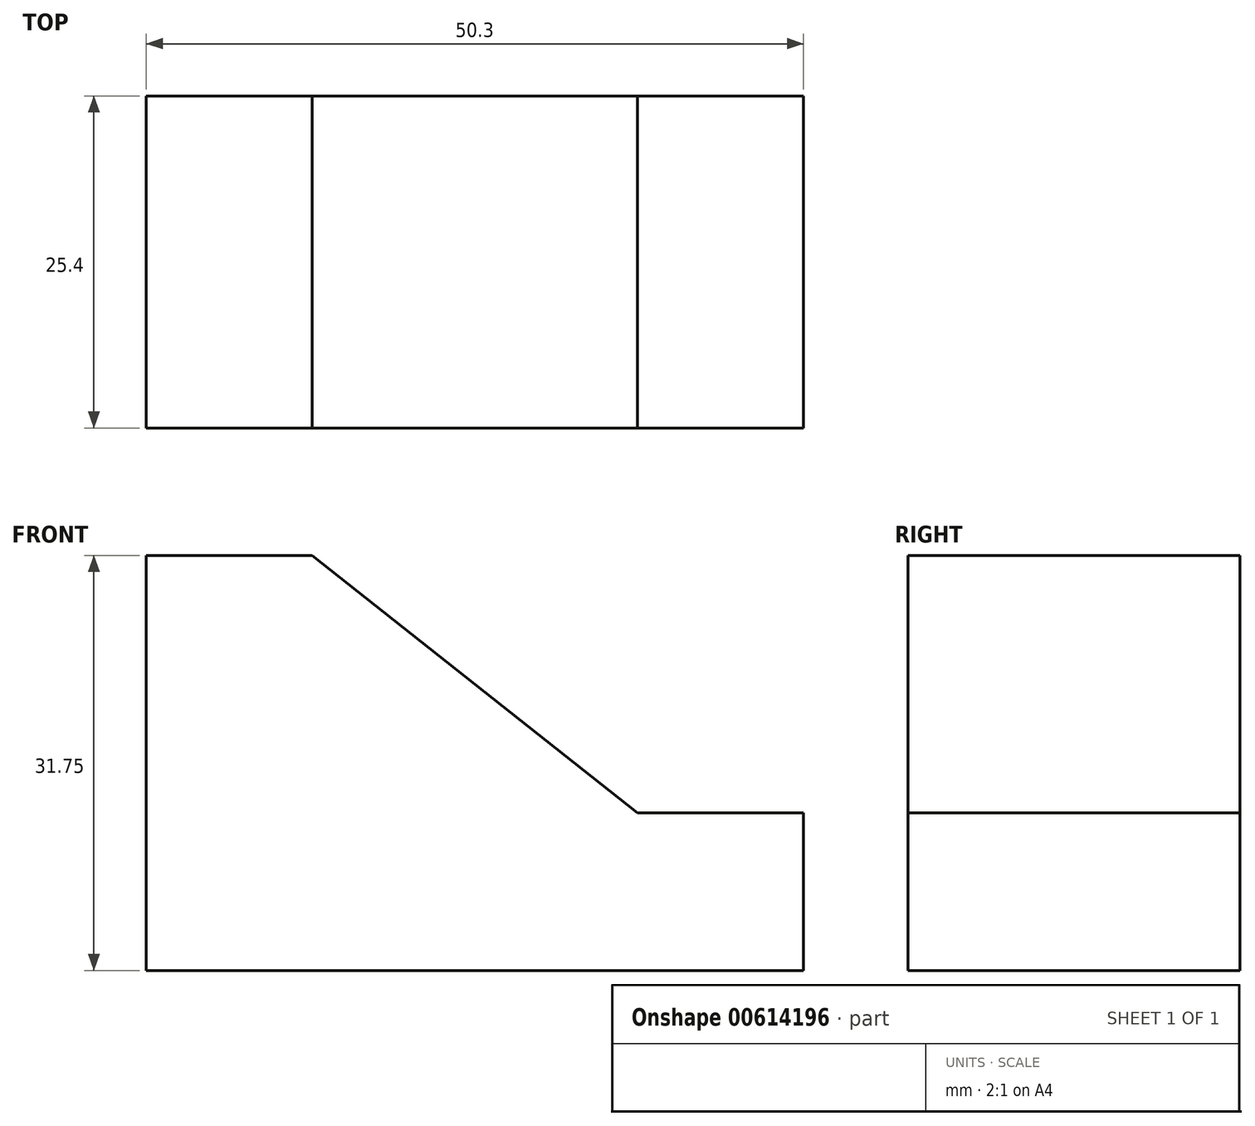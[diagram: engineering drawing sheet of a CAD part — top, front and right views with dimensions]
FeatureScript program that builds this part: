
annotation { "Feature Type Name" : "Feature", "Feature Type Description" : "" }
export const myFeature = defineFeature(function(context is Context, id is Id, definition is map)
    precondition{}
    {
        {
            var Q0;
            Q0=qCreatedBy(makeId("Front.planeOp"),FACE);
            var sketch = newSketch(context, id + "F0", { "sketchPlane" : qUnion([Q0])});
            skLineSegment(sketch, "E0", {"start": v(0, 0) * mm, "end": v(0, 31.75) * mm});
            skLineSegment(sketch, "E1", {"start": v(0, 31.75) * mm, "end": v(12.7, 31.75) * mm});
            skLineSegment(sketch, "E2", {"start": v(12.7, 31.75) * mm, "end": v(37.6, 12.05) * mm});
            skLineSegment(sketch, "E3", {"start": v(37.6, 12.05) * mm, "end": v(50.3, 12.05) * mm});
            skLineSegment(sketch, "E4", {"start": v(50.3, 12.05) * mm, "end": v(50.3, 0) * mm});
            skLineSegment(sketch, "E5", {"start": v(50.3, 0) * mm, "end": v(0, 0) * mm});
            skSolve(sketch);
        }
        {
            var Q0;
            Q0 = qSketchRegion(id + "F0", true);
            extrude(context, id + "F1", {"entities" : qUnion([Q0]), "depth" : 25.4 * mm, "offsetDistance" : 25.4 * mm});
        }
    });
